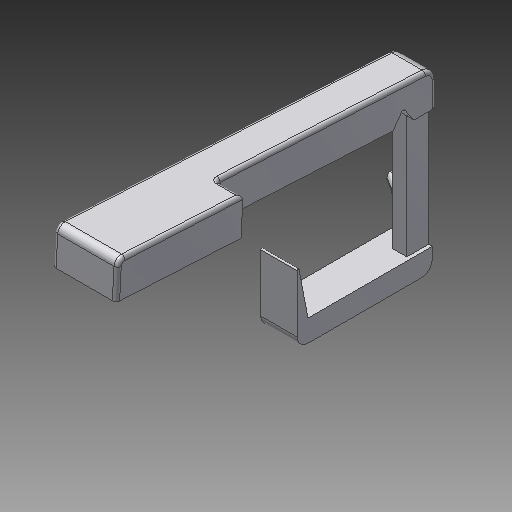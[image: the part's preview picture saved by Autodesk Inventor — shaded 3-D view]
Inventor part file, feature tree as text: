
AUTODESK INVENTOR PART (.ipt)
format: ipt  version: 2018 (Build 220112000, 112)  size: 316,928 bytes
history: native  units: mm
features: extrude x7, fillet x6, other x3, draft x1, chamfer x1
ambient origin geometry x8: Origin, YZ Plane, XZ Plane, XY Plane, X Axis, Y Axis, Z Axis, Center Point
bodies: Solid1 (feature_tree)
feature tree (18):
  other  "Key Sketch"
  extrude  "Upper Key"  Depth=10.0mm
  extrude  "Lower Key"  Depth=1.0mm
  other  "Hinge Cut Sketch"
  extrude  "Hinge Cut"  Depth=10.0mm TaperAngle=0.0deg
  extrude  "Hinge Cut 2"  Depth=3.0mm
  other  "Lever Sketch"
  extrude  "Vertical Lever"  Depth=3.0mm
  extrude  "Horizontal Lever"  Depth=33.6625mm
  extrude  "Spring Hook"  Depth=0.5mm
  draft  "FaceDraft3"
  chamfer  "Chamfer1"  Distance=3.0mm
  fillet  "Fillet9"  Radius=6.0mm
  fillet  "Fillet10"  Radius=4.0mm
  fillet  "Fillet5"  Radius=10.0mm
  fillet  "Fillet4"  [1 undecoded]
  fillet  "Fillet11"  Radius=3.0mm
  fillet  "Fillet14"  Radius=2.3mm
note: 1 required parameter value undecoded (feature->parameter linkage not recoverable at this tier; creation-order binding heuristic only, values carry confidence <= 0.55)
